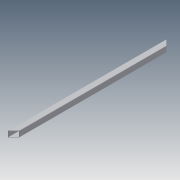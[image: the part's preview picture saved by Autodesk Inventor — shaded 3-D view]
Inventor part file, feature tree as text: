
AUTODESK INVENTOR PART (.ipt)
format: ipt  version: 2014 (Build 180170000, 170)  size: 107,008 bytes
history: native  units: in
note: dims shown in document units (in); Inventor stores cm internally (conversion verified against a paired STEP export)
features: extrude x2, sketch x2
ambient origin geometry x8: Origin, YZ Plane, XZ Plane, XY Plane, X Axis, Y Axis, Z Axis, Center Point
bodies: Solid1 (feature_tree)
feature tree (4):
  extrude  "Extrusion1"  Depth=1.0in
  extrude  "Extrusion2"  Depth=0.063in
  sketch  "Sketch1"  dims[d0=1.0in d1=1.0in]
  sketch  "Sketch2"  dims[d2=0.07in d3=0.063in d4=27.0in d5=0.0in d7=45.0deg d9=45.0deg d10=1.0in d11=0.0in]
